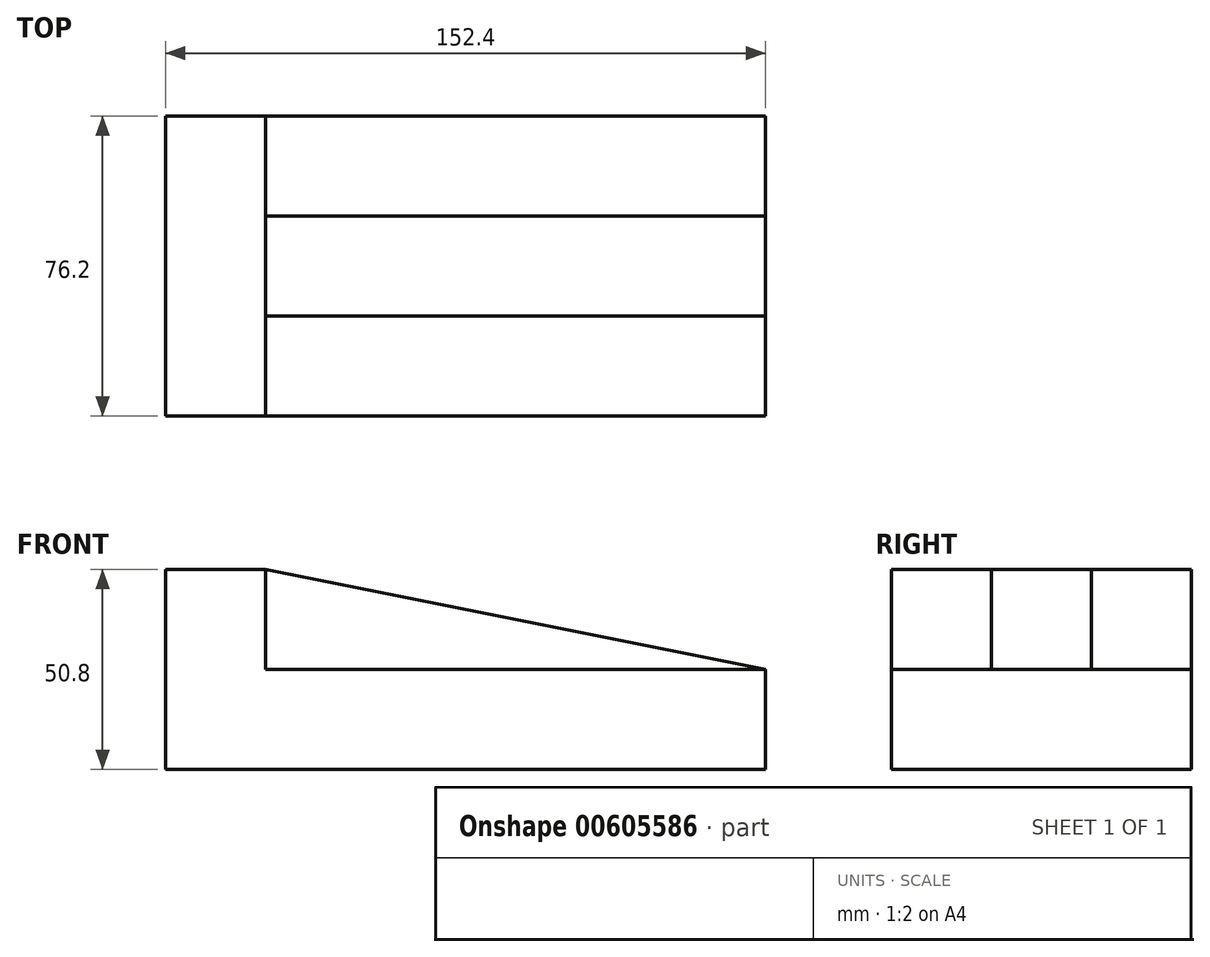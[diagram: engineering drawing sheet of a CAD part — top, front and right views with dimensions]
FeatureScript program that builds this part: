
annotation { "Feature Type Name" : "Feature", "Feature Type Description" : "" }
export const myFeature = defineFeature(function(context is Context, id is Id, definition is map)
    precondition{}
    {
        {
            var Q0;
            Q0=qCreatedBy(makeId("Top.planeOp"),FACE);
            var sketch = newSketch(context, id + "F0", { "sketchPlane" : qUnion([Q0])});
            skLineSegment(sketch, "E0", {"start": v(0, 0) * mm, "end": v(152.4, 0) * mm});
            skLineSegment(sketch, "E1", {"start": v(152.4, 0) * mm, "end": v(152.4, 76.2) * mm});
            skLineSegment(sketch, "E2", {"start": v(152.4, 76.2) * mm, "end": v(0, 76.2) * mm});
            skLineSegment(sketch, "E3", {"start": v(0, 76.2) * mm, "end": v(0, 0) * mm});
            skLineSegment(sketch, "E4.0", {"start": v(25.4, 76.2) * mm, "end": v(25.4, 0) * mm});
            skLineSegment(sketch, "E5.0", {"start": v(152.4, 50.8) * mm, "end": v(25.4, 50.8) * mm});
            skLineSegment(sketch, "E6.0", {"start": v(25.4, 25.4) * mm, "end": v(152.4, 25.4) * mm});
            skSolve(sketch);
        }
        {
            var Q0;
            {var subQ4=sQuery(id+"F0.wireOp",EDGE,"E3");Q0=makeQuery(id+"F0.imprint","IMPRINT",FACE,{"disambiguationData":[TD([[makeQuery(id+"F0.imprint","IMPRINT",EDGE,{"derivedFrom":subQ4}),1.0]])]});}
            extrude(context, id + "F1", {"entities" : qUnion([Q0]), "depth" : 50.8 * mm, "offsetDistance" : 25.4 * mm});
        }
        {
            var Q0;
            {var subQ5=sQuery(id+"F0.wireOp",EDGE,"E6.0");Q0=makeQuery(id+"F0.imprint","IMPRINT",FACE,{"disambiguationData":[TD([[makeQuery(id+"F0.imprint","IMPRINT",EDGE,{"derivedFrom":subQ5}),-1.0]])]});}
            var Q1;
            {var subQ3=sQuery(id+"F0.wireOp",EDGE,"E5.0");Q1=makeQuery(id+"F0.imprint","IMPRINT",FACE,{"disambiguationData":[TD([[makeQuery(id+"F0.imprint","IMPRINT",EDGE,{"derivedFrom":subQ3}),-1.0]])]});}
            extrude(context, id + "F2", {"entities" : qUnion([Q0, Q1]), "operationType" : NewBodyOperationType.ADD, "depth" : 25.4 * mm, "offsetDistance" : 25.4 * mm});
        }
        {
            var Q0;
            {var subQ0=sQuery(id+"F0.wireOp",EDGE,"E5.0");Q0=makeQuery(id+"F0.imprint","IMPRINT",FACE,{"disambiguationData":[TD([[makeQuery(id+"F0.imprint","IMPRINT",EDGE,{"derivedFrom":subQ0}),1.0]])]});}
            extrude(context, id + "F3", {"entities" : qUnion([Q0]), "operationType" : NewBodyOperationType.ADD, "depth" : 50.8 * mm, "offsetDistance" : 25.4 * mm});
        }
        {
            var Q0;
            Q0=makeQuery(id+"F3.opExtrude","SWEPT_FACE",FACE,{"disambiguationData":[OSD([sQuery(id+"F0.wireOp",EDGE,"E6.0")])]});
            var sketch = newSketch(context, id + "F4", { "sketchPlane" : qUnion([Q0])});
            skLineSegment(sketch, "E7", {"start": v(25.4, 50.8) * mm, "end": v(152.4, 25.4) * mm});
            skSolve(sketch);
        }
        {
            var Q0;
            Q0=makeQuery(id+"F4.imprint","IMPRINT",FACE,{"disambiguationData":[TD([[makeQuery(id+"F4.imprint","IMPRINT",EDGE,{"derivedFrom":sQuery(id+"F4.wireOp",EDGE,"E7")}),1.0]])]});
            extrude(context, id + "F5", {"entities" : qUnion([Q0]), "operationType" : NewBodyOperationType.REMOVE, "oppositeDirection" : true, "depth" : 25.4 * mm, "offsetDistance" : 25.4 * mm});
        }
    });
